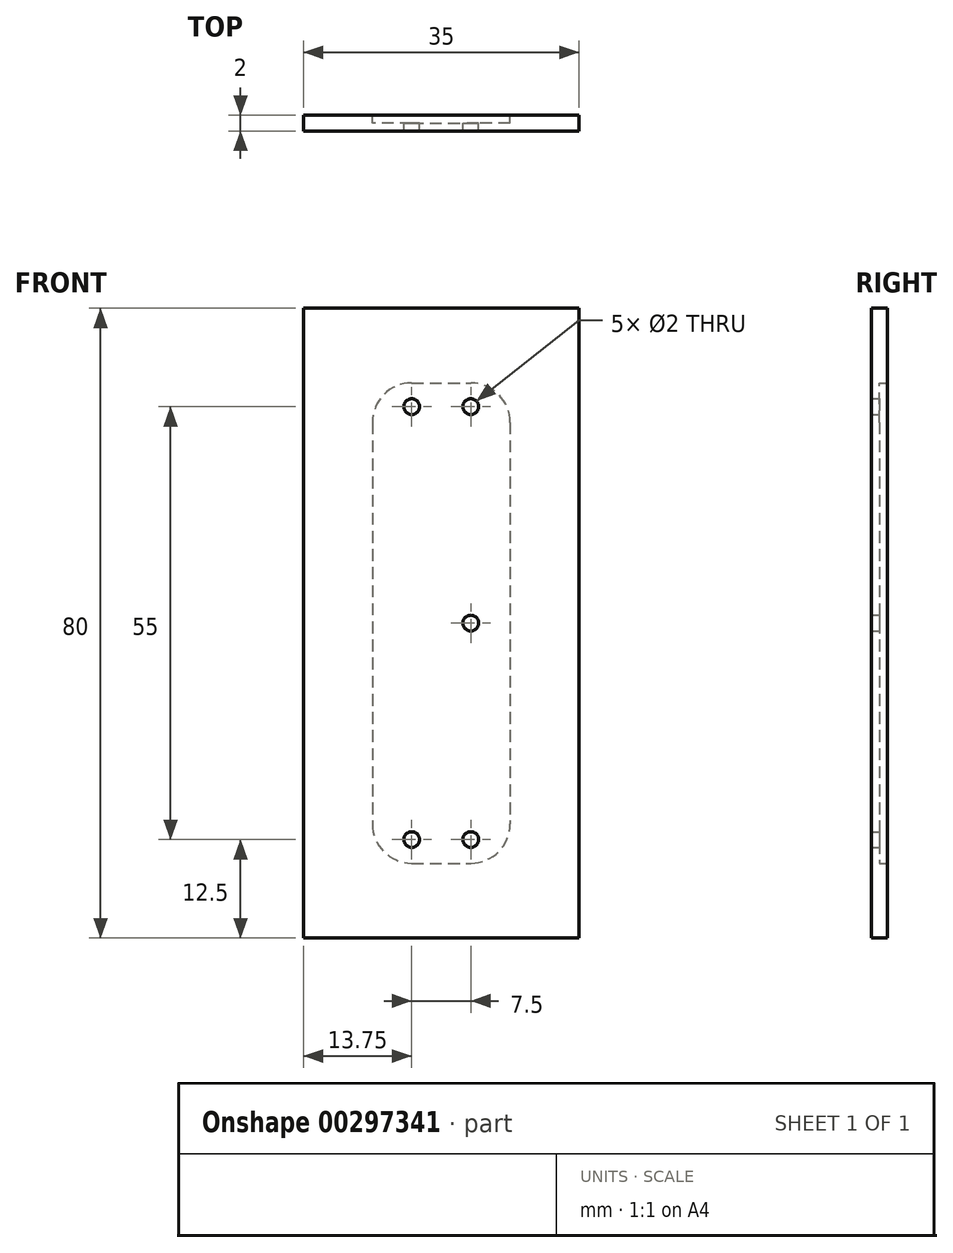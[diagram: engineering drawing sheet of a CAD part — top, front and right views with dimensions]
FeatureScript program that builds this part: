
annotation { "Feature Type Name" : "Feature", "Feature Type Description" : "" }
export const myFeature = defineFeature(function(context is Context, id is Id, definition is map)
    precondition{}
    {
        {
            var Q0;
            Q0=qCreatedBy(makeId("Front.planeOp"),FACE);
            var sketch = newSketch(context, id + "F0", { "sketchPlane" : qUnion([Q0])});
            skLineSegment(sketch, "E0.bottom", {"start": v(17.5, 40) * mm, "end": v(-17.5, 40) * mm});
            skLineSegment(sketch, "E0.top", {"start": v(17.5, -40) * mm, "end": v(-17.5, -40) * mm});
            skLineSegment(sketch, "E0.left", {"start": v(17.5, 40) * mm, "end": v(17.5, -40) * mm});
            skLineSegment(sketch, "E0.right", {"start": v(-17.5, 40) * mm, "end": v(-17.5, -40) * mm});
            skPoint(sketch, "E0.middle", {"position": v(0, 0) * mm});
            skSolve(sketch);
        }
        {
            var Q0;
            Q0=qSketchRegion(id+"F0",true);
            extrude(context, id + "F1", {"entities" : qUnion([Q0]), "depth" : 2 * mm});
        }
        {
            var Q0;
            Q0=makeQuery(id+"F1.opExtrude","CAP_FACE",FACE,{"disambiguationData":[OSD([sQuery(id+"F0.wireOp",EDGE,"E0.bottom"),sQuery(id+"F0.wireOp",EDGE,"E0.top"),sQuery(id+"F0.wireOp",EDGE,"E0.left"),sQuery(id+"F0.wireOp",EDGE,"E0.right")])],"isStart":true});
            var sketch = newSketch(context, id + "F2", { "sketchPlane" : qUnion([Q0])});
            skLineSegment(sketch, "E1.bottom", {"start": v(8.75, 30.5) * mm, "end": v(-8.75, 30.5) * mm});
            skLineSegment(sketch, "E1.top", {"start": v(8.75, -30.5) * mm, "end": v(-8.75, -30.5) * mm});
            skLineSegment(sketch, "E1.left", {"start": v(8.75, 30.5) * mm, "end": v(8.75, -30.5) * mm});
            skLineSegment(sketch, "E1.right", {"start": v(-8.75, 30.5) * mm, "end": v(-8.75, -30.5) * mm});
            skPoint(sketch, "E1.middle", {"position": v(0, 0) * mm});
            skSolve(sketch);
        }
        {
            var Q0;
            Q0 = qSketchRegion(id + "F2", true);
            extrude(context, id + "F3", {"entities" : qUnion([Q0]), "operationType" : NewBodyOperationType.REMOVE, "oppositeDirection" : true, "depth" : 1 * mm});
        }
        {
            var Q0;
            Q0=makeQuery(id+"F3.boolean.opBoolean","COPY",FACE,{"derivedFrom":makeQuery(id+"F3.opExtrude","CAP_FACE",FACE,{"disambiguationData":[OSD([sQuery(id+"F2.wireOp",EDGE,"E1.bottom"),sQuery(id+"F2.wireOp",EDGE,"E1.top"),sQuery(id+"F2.wireOp",EDGE,"E1.left"),sQuery(id+"F2.wireOp",EDGE,"E1.right")])],"isStart":false})});
            var sketch = newSketch(context, id + "F4", { "sketchPlane" : qUnion([Q0])});
            skLineSegment(sketch, "E2.bottom", {"start": v(3.75, 27.5) * mm, "end": v(-3.75, 27.5) * mm, "construction": true});
            skLineSegment(sketch, "E2.top", {"start": v(3.75, -27.5) * mm, "end": v(-3.75, -27.5) * mm, "construction": true});
            skLineSegment(sketch, "E2.left", {"start": v(3.75, 27.5) * mm, "end": v(3.75, -27.5) * mm, "construction": true});
            skLineSegment(sketch, "E2.right", {"start": v(-3.75, 27.5) * mm, "end": v(-3.75, -27.5) * mm, "construction": true});
            skPoint(sketch, "E2.middle", {"position": v(0, 0) * mm});
            skCircle(sketch, "E3", {"center": v(-3.75, 27.5) * mm, "radius": 1 * mm});
            skCircle(sketch, "E4", {"center": v(-3.75, 0) * mm, "radius": 1 * mm});
            skCircle(sketch, "E5", {"center": v(-3.75, -27.5) * mm, "radius": 1 * mm});
            skCircle(sketch, "E6", {"center": v(3.75, 27.5) * mm, "radius": 1 * mm});
            skCircle(sketch, "E7", {"center": v(3.75, -27.5) * mm, "radius": 1 * mm});
            skSolve(sketch);
        }
        {
            var Q0;
            Q0 = qSketchRegion(id + "F4", true);
            extrude(context, id + "F5", {"entities" : qUnion([Q0]), "operationType" : NewBodyOperationType.REMOVE, "oppositeDirection" : true, "depth" : 25 * mm});
        }
        {
            var Q0;
            Q0=makeQuery(id+"F3.boolean.opBoolean","COPY",EDGE,{"derivedFrom":makeQuery(id+"F3.opExtrude","SWEPT_EDGE",EDGE,{"disambiguationData":[OSD([sQuery(id+"F2.wireOp",EDGE,"E1.bottom"),sQuery(id+"F2.wireOp",EDGE,"E1.left")])]})});
            var Q1;
            Q1=makeQuery(id+"F3.boolean.opBoolean","COPY",EDGE,{"derivedFrom":makeQuery(id+"F3.opExtrude","SWEPT_EDGE",EDGE,{"disambiguationData":[OSD([sQuery(id+"F2.wireOp",EDGE,"E1.bottom"),sQuery(id+"F2.wireOp",EDGE,"E1.right")])]})});
            var Q2;
            Q2=makeQuery(id+"F3.boolean.opBoolean","COPY",EDGE,{"derivedFrom":makeQuery(id+"F3.opExtrude","SWEPT_EDGE",EDGE,{"disambiguationData":[OSD([sQuery(id+"F2.wireOp",EDGE,"E1.top"),sQuery(id+"F2.wireOp",EDGE,"E1.left")])]})});
            var Q3;
            Q3=makeQuery(id+"F3.boolean.opBoolean","COPY",EDGE,{"derivedFrom":makeQuery(id+"F3.opExtrude","SWEPT_EDGE",EDGE,{"disambiguationData":[OSD([sQuery(id+"F2.wireOp",EDGE,"E1.top"),sQuery(id+"F2.wireOp",EDGE,"E1.right")])]})});
            fillet(context, id + "F6", {"entities" : qUnion([Q0, Q1, Q2, Q3]), "radius" : 5 * mm, "tangentPropagation" : true, "allowEdgeOverflow" : false});
        }
    });
